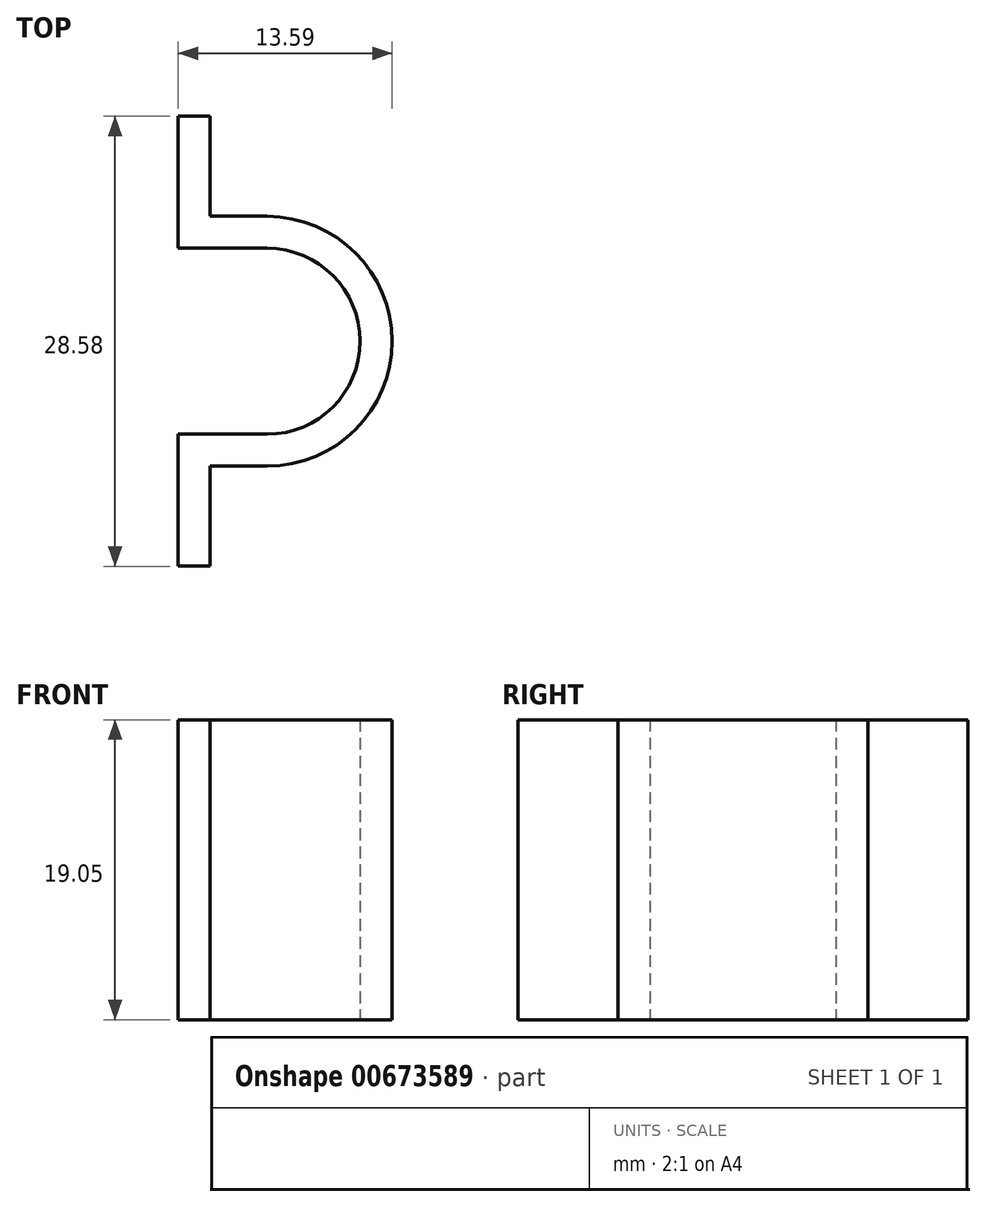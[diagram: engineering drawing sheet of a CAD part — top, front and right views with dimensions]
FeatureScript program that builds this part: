
annotation { "Feature Type Name" : "Feature", "Feature Type Description" : "" }
export const myFeature = defineFeature(function(context is Context, id is Id, definition is map)
    precondition{}
    {
        {
            var Q0;
            Q0=qCreatedBy(makeId("Top.planeOp"),FACE);
            var sketch = newSketch(context, id + "F0", { "sketchPlane" : qUnion([Q0])});
            skPoint(sketch, "E0.orphan", {"position": v(0, -9.61) * mm});
            skLineSegment(sketch, "E1", {"start": v(0, 5.9) * mm, "end": v(-5.65, 5.9) * mm});
            skLineSegment(sketch, "E2", {"start": v(0, -5.9) * mm, "end": v(-5.65, -5.9) * mm});
            skLineSegment(sketch, "E3", {"start": v(0, -7.94) * mm, "end": v(-3.62, -7.94) * mm});
            skLineSegment(sketch, "E4", {"start": v(0, 7.94) * mm, "end": v(-3.62, 7.94) * mm});
            skLineSegment(sketch, "E5", {"start": v(-5.65, -7.94) * mm, "end": v(-5.65, -5.9) * mm});
            skPoint(sketch, "E6.orphan", {"position": v(-10.42, 7.94) * mm});
            skPoint(sketch, "E7.orphan", {"position": v(-10.42, 5.9) * mm});
            skPoint(sketch, "E8.orphan", {"position": v(-14.69, -5.9) * mm});
            skPoint(sketch, "E9.orphan", {"position": v(-14.69, -7.94) * mm});
            skLineSegment(sketch, "E10", {"start": v(-5.65, 5.9) * mm, "end": v(-5.65, 7.94) * mm});
            skLineSegment(sketch, "E11", {"start": v(-5.65, -5.9) * mm, "end": v(-5.65, 5.9) * mm, "construction": true});
            skLineSegment(sketch, "E12", {"start": v(-5.9, 0) * mm, "end": v(-5.65, 0) * mm, "construction": true});
            skArc(sketch, "E13", {"start": v(0, 5.9) * mm, "mid": v(-5.9, 0) * mm, "end": v(0, -5.9) * mm, "construction": true});
            skArc(sketch, "E14", {"start": v(0, -5.9) * mm, "mid": v(5.9, 0) * mm, "end": v(0, 5.9) * mm});
            skArc(sketch, "E15", {"start": v(0, -7.94) * mm, "mid": v(7.94, 0) * mm, "end": v(0, 7.94) * mm});
            skLineSegment(sketch, "E16", {"start": v(-5.65, 7.94) * mm, "end": v(-5.65, 14.29) * mm});
            skLineSegment(sketch, "E17", {"start": v(-5.65, 14.29) * mm, "end": v(-3.62, 14.29) * mm});
            skLineSegment(sketch, "E18", {"start": v(-3.62, 14.29) * mm, "end": v(-3.62, 7.94) * mm});
            skLineSegment(sketch, "E19", {"start": v(-5.65, -7.94) * mm, "end": v(-5.65, -14.29) * mm});
            skLineSegment(sketch, "E20", {"start": v(-5.65, -14.29) * mm, "end": v(-3.62, -14.29) * mm});
            skLineSegment(sketch, "E21", {"start": v(-3.62, -14.29) * mm, "end": v(-3.62, -7.94) * mm});
            skSolve(sketch);
        }
        {
            var Q0;
            Q0 = qSketchRegion(id + "F0", true);
            extrude(context, id + "F1", {"entities" : qUnion([Q0]), "depth" : 19.05 * mm, "offsetDistance" : 25.4 * mm});
        }
    });
